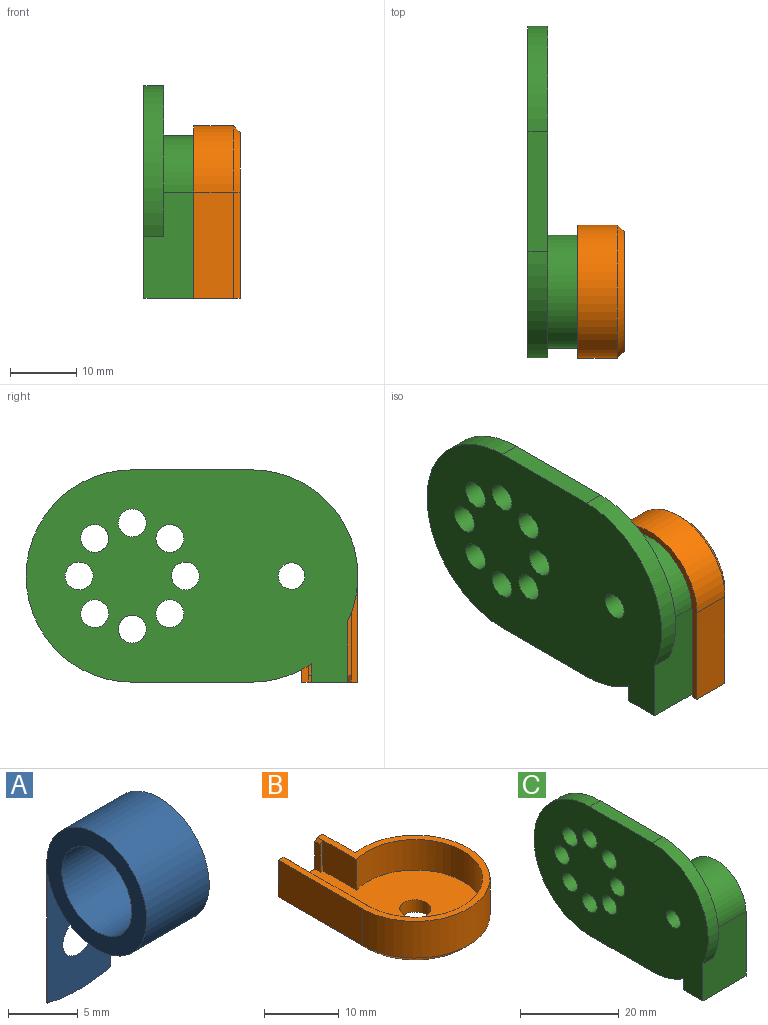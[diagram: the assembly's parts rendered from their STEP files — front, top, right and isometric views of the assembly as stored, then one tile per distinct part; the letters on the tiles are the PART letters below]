
ASSEMBLY  parts=3 mates=2
PART A: 8 faces, bbox 6.4x10.2x17.8 mm
  f0: plane 17.38x10.16mm, normal (1,0,0), area 42.5mm2, adj f2,f3,f4,f5,f6
  f1: plane 17.38x10.16mm, normal (-1,0,0), area 42.5mm2, adj f2,f3,f4,f5,f6
  f2: cylinder r=5.08mm len=10.16mm, axis (-1,0,0), area 196.2mm2, adj f0,f1,f3,f4
  f3: plane 11.69x6.35mm, normal (0,-1,0), area 64.8mm2, adj f0,f1,f2,f6,f7
  f4: plane 12.7x6.35mm, normal (0,1,0), area 71.2mm2, adj f0,f1,f2,f6,f7
  f5: cylinder r=3.56mm len=7.11mm, axis (-1,0,0), area 141.9mm2, adj f0,f1
  f6: cylinder r=12.7mm len=6.35mm, axis (0,1,0), area 0.7mm2, adj f0,f1,f3,f4
  f7: cylinder r=1.65mm len=3.3mm, axis (0,1,0), area 1.1mm2, adj f3,f4
PART B: 24 faces, bbox 20x26x7 mm
  f0: plane 6.35x5mm, normal (-1,0,0), area 31.8mm2, adj f2,f3,f4,f16
  f1: plane 13x5mm, normal (1,0,0), area 65mm2, adj f2,f3,f11,f14
  f2: plane 25x18mm, normal (0,0,1), area 301.7mm2, adj f0,f1,f4,f6,f8,f11,f12,f13
  f3: plane 26x20mm, normal (0,0,1), area 69.5mm2, adj f0,f1,f4,f5,f8,f9,f10,f18
  f4: cylinder r=9mm len=18mm, axis (0,0,1), area 229.7mm2, adj f0,f2,f3,f12,f20
  f5: cylinder r=10mm len=20mm, axis (0,0,-1), area 291.8mm2, adj f3,f9,f10,f22
  f6: cylinder r=2.1mm len=4.2mm, axis (0,0,-1), area 26.4mm2, adj f2,f7
  f7: plane 25x18mm, normal (0,0,-1), area 303.2mm2, adj f6,f8,f21,f22,f23
  f8: plane 8.5x7mm, normal (0,1,0), area 30.7mm2, adj f2,f3,f7,f9,f10,f15,f17,f18
  f9: plane 16x6mm, normal (-1,0,0), area 96mm2, adj f3,f5,f8,f23
  f10: plane 6.11x6mm, normal (1,0,0), area 36.7mm2, adj f3,f5,f8,f21
  f11: plane 5x0.5mm, normal (0,1,0), area 2.4mm2, adj f1,f2,f13,f20
  f12: plane 4.94x0.44mm, normal (0,-1,0), area 2.1mm2, adj f2,f4,f13,f20
  f13: plane 4.5x1mm, normal (1,0,0), area 4.5mm2, adj f2,f11,f12,f20
  f14: plane 5x0.5mm, normal (0,-1,0), area 2.4mm2, adj f1,f2,f15,f19
  f15: plane 4.5x1mm, normal (1,0,0), area 4.5mm2, adj f2,f8,f14,f19
  f16: plane 5x0.5mm, normal (0,-1,0), area 2.4mm2, adj f0,f2,f17,f18
  f17: plane 4.5x1mm, normal (-1,0,0), area 4.5mm2, adj f2,f8,f16,f18
  f18: plane 1x0.5mm, normal (-0.71,0,0.71), area 0.7mm2, adj f3,f8,f16,f17
  f19: plane 1x0.5mm, normal (0.71,0,0.71), area 0.7mm2, adj f3,f8,f14,f15
  f20: plane 2x0.5mm, normal (0.71,0,0.71), area 0.7mm2, adj f3,f4,f11,f12,f13
  f21: plane 7.35x1mm, normal (0.71,0,-0.71), area 9.5mm2, adj f7,f8,f10,f22
  f22: cone r=10mm half-angle=45deg, axis (0,0,1), area 66.2mm2, adj f5,f7,f21,f23
  f23: plane 16x1mm, normal (-0.71,0,-0.71), area 22.6mm2, adj f7,f8,f9,f22
PART C: 27 faces, bbox 12.4x50x32 mm
  f0: plane 18x3mm, normal (0,0,-1), area 54mm2, adj f3,f4,f16,f21
  f1: plane 5.5x3mm, normal (0,0,-1), area 16.5mm2, adj f3,f8,f9,f12
  f2: plane 18x3mm, normal (0,0,1), area 54mm2, adj f3,f4,f21,f22
  f3: plane 50x32mm, normal (-1,0,0), area 1286.6mm2, adj f0,f1,f2,f8,f9,f13,f16,f17
  f4: plane 50x32mm, normal (1,0,0), area 1016mm2, adj f0,f2,f5,f8,f9,f16,f17,f18
  f5: cylinder r=8.5mm len=17mm, axis (-1,0,0), area 403.2mm2, adj f4,f6,f8,f9
  f6: plane 24.5x17mm, normal (1,0,0), area 97.6mm2, adj f5,f7,f8,f9,f10,f11,f14,f15
  f7: cylinder r=7mm len=14mm, axis (1,0,0), area 354.1mm2, adj f6,f10,f11,f12
  f8: plane 12.35x8.05mm, normal (0,1,0), area 83.6mm2, adj f1,f3,f4,f5,f6,f15,f16
  f9: plane 16x12.35mm, normal (0,-1,0), area 177.3mm2, adj f1,f3,f4,f5,f6,f14,f22
  f10: plane 14.5x9.35mm, normal (0,1,0), area 135.6mm2, adj f6,f7,f12,f14
  f11: plane 9.35x9.14mm, normal (0,-1,0), area 85.4mm2, adj f6,f7,f12,f15
  f12: plane 23x15.5mm, normal (1,0,0), area 173mm2, adj f1,f7,f10,f11,f13,f14,f15
  f13: cylinder r=2mm len=4mm, axis (1,0,0), area 37.7mm2, adj f3,f12
  f14: cylinder r=1.5mm len=9.35mm, axis (-1,0,0), area 22mm2, adj f6,f9,f10,f12
  f15: cylinder r=1.5mm len=9.35mm, axis (-1,0,0), area 22mm2, adj f6,f8,f11,f12
  f16: cylinder r=16mm len=9mm, axis (1,0,0), area 28.7mm2, adj f0,f3,f4,f8
  f17: cylinder r=2.1mm len=4.2mm, axis (1,0,0), area 39.6mm2, adj f3,f4
  f18: cylinder r=2.1mm len=4.2mm, axis (1,0,0), area 39.6mm2, adj f3,f4
  f19: cylinder r=2.1mm len=4.2mm, axis (1,0,0), area 39.6mm2, adj f3,f4
  f20: cylinder r=2.1mm len=4.2mm, axis (1,0,0), area 39.6mm2, adj f3,f4
  f21: cylinder r=16mm len=32mm, axis (1,0,0), area 150.8mm2, adj f0,f2,f3,f4
  f22: cylinder r=16mm len=22.76mm, axis (1,0,0), area 96.3mm2, adj f2,f3,f4,f9
  f23: cylinder r=2.1mm len=4.2mm, axis (1,0,0), area 39.6mm2, adj f3,f4
  f24: cylinder r=2.1mm len=4.2mm, axis (1,0,0), area 39.6mm2, adj f3,f4
  f25: cylinder r=2.1mm len=4.2mm, axis (1,0,0), area 39.6mm2, adj f3,f4
  f26: cylinder r=2.1mm len=4.2mm, axis (1,0,0), area 39.6mm2, adj f3,f4
PLACE A rot(axis=(0,0,1),180deg) t=(-9.37,-21.56,-1.14)mm
PLACE B rot(axis=(-0.58,-0.58,0.58),120deg) t=(-2.55,-21.56,-1.14)mm
PLACE C t=(-14.05,-21.56,-1.14)mm
MATE fastened B.f4 <-> A.f2  axis (-1,0,0) through (-4.55,-21.56,-1.14)mm
MATE fastened A.f2 <-> C.f5  axis (-1,0,0) through (-12.55,-21.56,-1.14)mm
